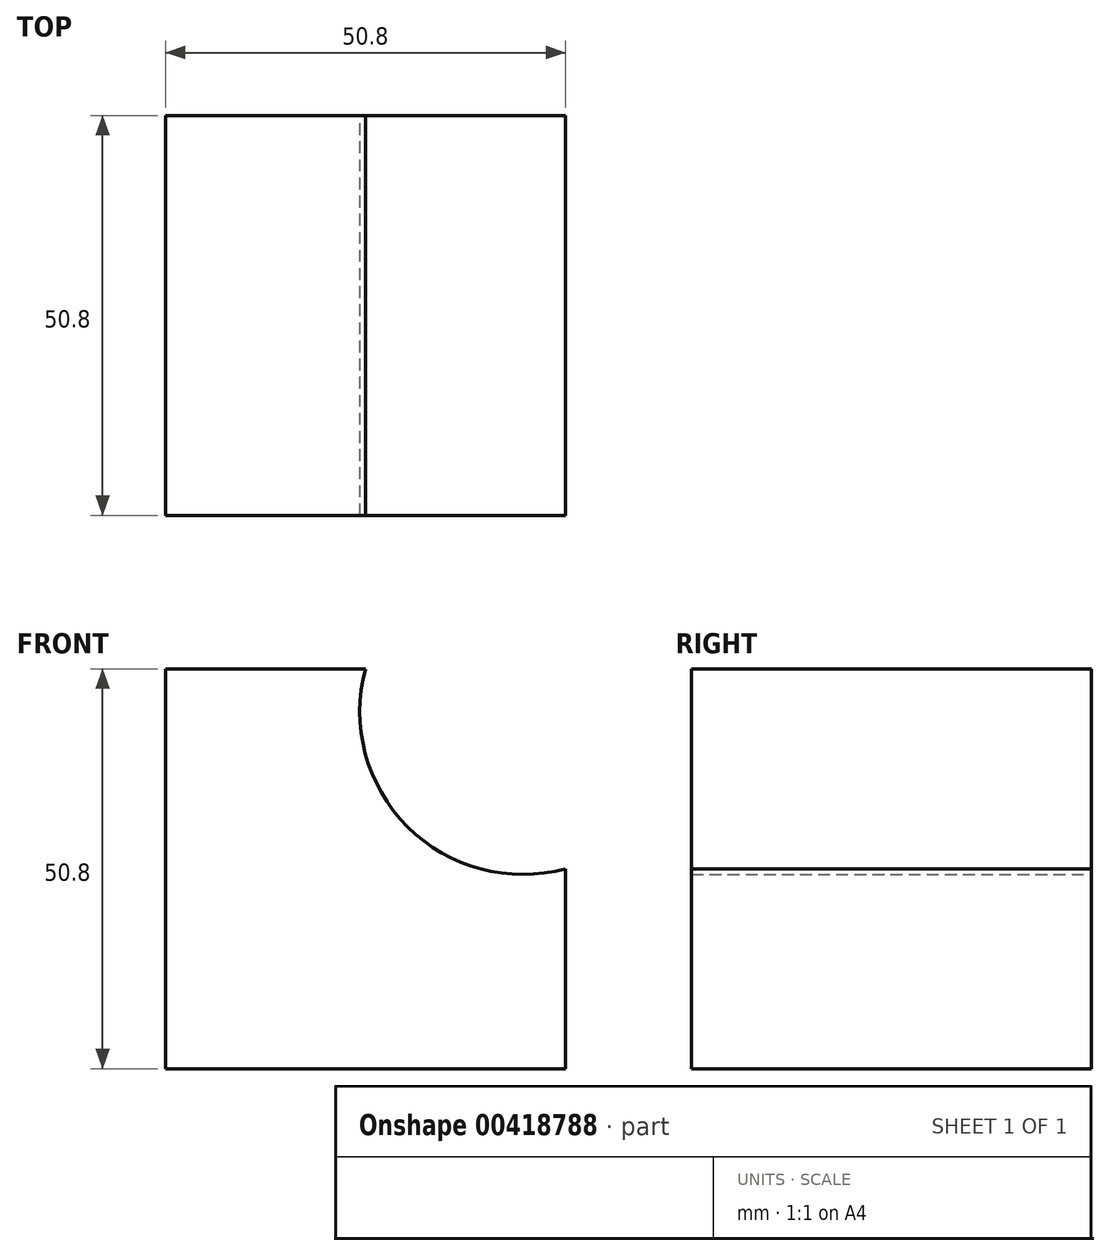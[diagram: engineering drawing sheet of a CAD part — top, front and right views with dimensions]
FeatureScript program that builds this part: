
annotation { "Feature Type Name" : "Feature", "Feature Type Description" : "" }
export const myFeature = defineFeature(function(context is Context, id is Id, definition is map)
    precondition{}
    {
        {
            var Q0;
            Q0=qCreatedBy(makeId("Front.planeOp"),FACE);
            var sketch = newSketch(context, id + "F0", { "sketchPlane" : qUnion([Q0])});
            skLineSegment(sketch, "E0", {"start": v(0, 0) * mm, "end": v(-25.4, 0) * mm});
            skLineSegment(sketch, "E1", {"start": v(-25.4, 0) * mm, "end": v(-25.4, -50.8) * mm});
            skLineSegment(sketch, "E2", {"start": v(-25.4, -50.8) * mm, "end": v(25.4, -50.8) * mm});
            skLineSegment(sketch, "E3", {"start": v(25.4, -50.8) * mm, "end": v(25.4, -25.4) * mm});
            skArc(sketch, "E4", {"start": v(0, 0) * mm, "mid": v(5.33, -20.07) * mm, "end": v(25.4, -25.4) * mm});
            skSolve(sketch);
        }
        {
            var Q0;
            Q0=makeQuery(id+"F0.imprint","IMPRINT",FACE,{"disambiguationData":[TD([[makeQuery(id+"F0.imprint","IMPRINT",EDGE,{"derivedFrom":sQuery(id+"F0.wireOp",EDGE,"E0")}),1.0]])]});
            extrude(context, id + "F1", {"entities" : qUnion([Q0]), "depth" : 50.8 * mm});
        }
    });
